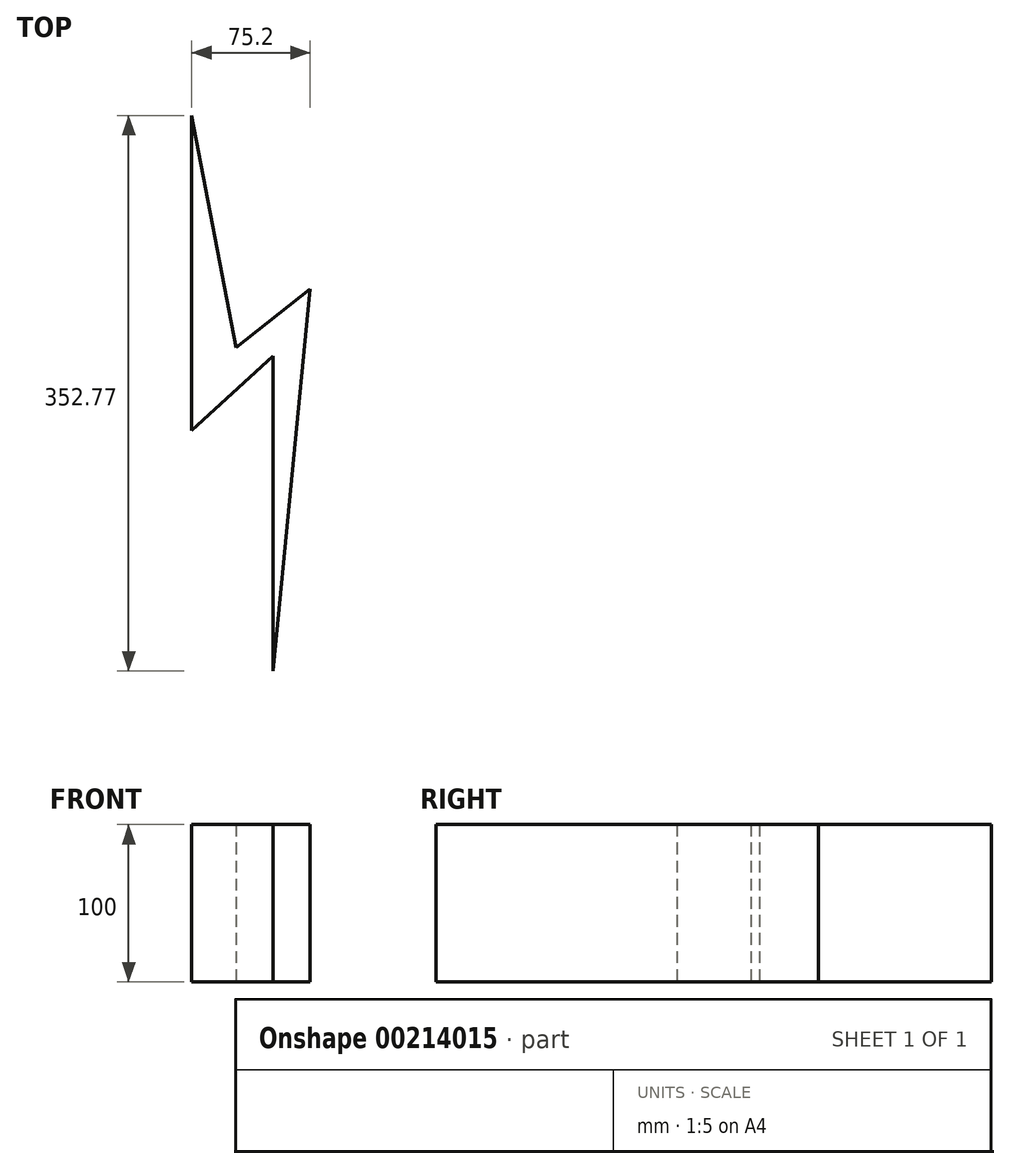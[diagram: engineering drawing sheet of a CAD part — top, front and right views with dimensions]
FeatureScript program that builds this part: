
annotation { "Feature Type Name" : "Feature", "Feature Type Description" : "" }
export const myFeature = defineFeature(function(context is Context, id is Id, definition is map)
    precondition{}
    {
        {
            var Q0;
            Q0=qCreatedBy(makeId("Top.planeOp"),FACE);
            var sketch = newSketch(context, id + "F0", { "sketchPlane" : qUnion([Q0])});
            skLineSegment(sketch, "E0", {"start": v(92.41, 302.1) * mm, "end": v(92.41, 102.1) * mm});
            skLineSegment(sketch, "E1", {"start": v(92.41, 102.1) * mm, "end": v(144.08, 149.32) * mm});
            skLineSegment(sketch, "E2", {"start": v(144.08, 149.32) * mm, "end": v(144.08, -50.68) * mm});
            skLineSegment(sketch, "E3", {"start": v(92.41, 302.1) * mm, "end": v(120.58, 154.76) * mm});
            skLineSegment(sketch, "E4", {"start": v(120.58, 154.76) * mm, "end": v(167.6, 192.02) * mm});
            skLineSegment(sketch, "E5", {"start": v(167.6, 192.02) * mm, "end": v(144.08, -50.68) * mm});
            skSolve(sketch);
        }
        {
            var Q0;
            Q0=makeQuery(id+"F0.imprint","IMPRINT",FACE,{"disambiguationData":[TD([[makeQuery(id+"F0.imprint","IMPRINT",EDGE,{"derivedFrom":sQuery(id+"F0.wireOp",EDGE,"E0")}),1.0]])]});
            extrude(context, id + "F1", {"entities" : qUnion([Q0]), "depth" : 100 * mm});
        }
    });
